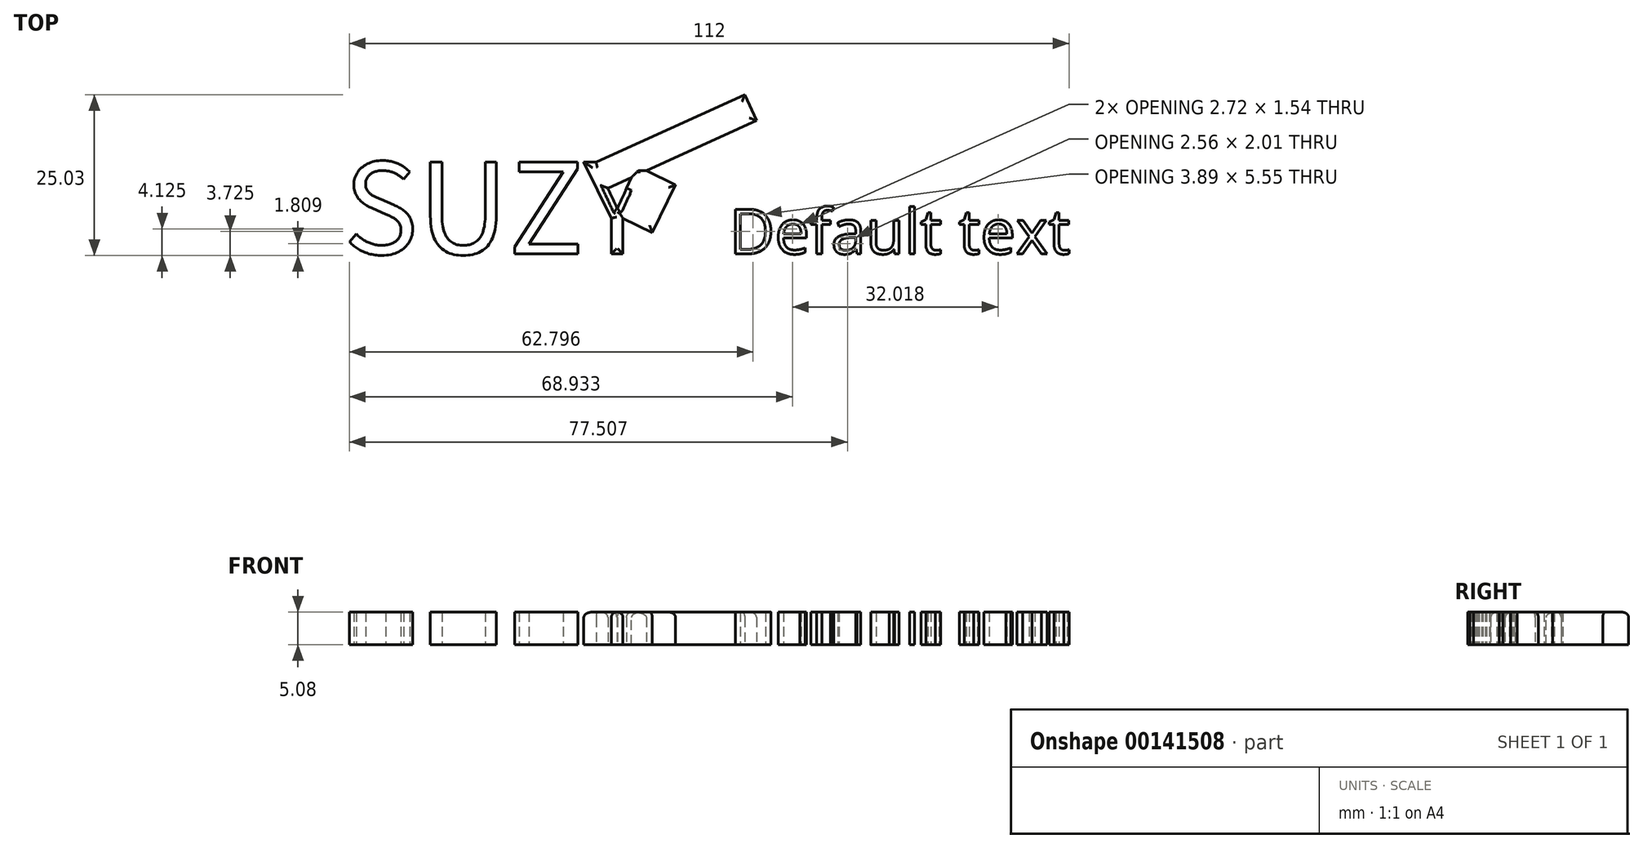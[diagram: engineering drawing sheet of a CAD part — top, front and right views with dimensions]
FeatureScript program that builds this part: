
annotation { "Feature Type Name" : "Feature", "Feature Type Description" : "" }
export const myFeature = defineFeature(function(context is Context, id is Id, definition is map)
    precondition{}
    {
        {
            var Q0;
            Q0=qCreatedBy(makeId("Top.planeOp"),FACE);
            var sketch = newSketch(context, id + "F0", { "sketchPlane" : qUnion([Q0])});
            skText(sketch, "E0", { "text": "SUZY", "fontName": "NotoSansCJKjp-Regular.otf"});
            skText(sketch, "E1", { "text": "Default text", "fontName": "OpenSans-Regular.ttf"});
            skPoint(sketch, "E1.secondSnap0", {"position": v(19.76, 18.92) * mm});
            const initialGuessF0  = {"E0": [-0.0291, 0.01191, 1, 0, 0.01402], "E1": [0.03091, 0.01191, 1, 0, 0.00701]};
            skSetInitialGuess(sketch, initialGuessF0);
            skSolve(sketch);
        }
        {
            var Q0;
            Q0 = qSketchRegion(id + "F0", true);
            extrude(context, id + "F1", {"entities" : qUnion([Q0]), "depth" : 5.08 * mm});
        }
        {
            var Q0;
            Q0=makeQuery(id+"F1.opExtrude","SWEPT_FACE",FACE,{"disambiguationData":[OSD([sQuery(id+"F0.wireOp",EDGE,"E0.sketch_text.stroke-44")])]});
            extrude(context, id + "F2", {"entities" : qUnion([Q0]), "operationType" : NewBodyOperationType.ADD, "depth" : 25.4 * mm});
        }
        {
            var Q0;
            Q0=makeQuery(id+"F1.opExtrude","SWEPT_FACE",FACE,{"disambiguationData":[OSD([sQuery(id+"F0.wireOp",EDGE,"E0.sketch_text.stroke-38")])]});
            extrude(context, id + "F3", {"entities" : qUnion([Q0]), "operationType" : NewBodyOperationType.ADD, "depth" : 5.08 * mm});
        }
        {
            var Q0;
            {var subQ0=sQuery(id+"F0.wireOp",EDGE,"E0.sketch_text.stroke-38");var subQ1=sQuery(id+"F0.wireOp",EDGE,"E0.sketch_text.stroke-44");Q0=makeQuery(id+"F3.boolean.opBoolean","MERGE",FACE,{"derivedFrom":[makeQuery(id+"F2.boolean.opBoolean","MERGE",FACE,{"derivedFrom":[makeQuery(id+"F1.opExtrude","CAP_FACE",FACE,{"disambiguationData":[OSD([sQuery(id+"F0.wireOp",EDGE,"E0.sketch_text.stroke-36"),sQuery(id+"F0.wireOp",EDGE,"E0.sketch_text.stroke-37"),subQ0,sQuery(id+"F0.wireOp",EDGE,"E0.sketch_text.stroke-39"),sQuery(id+"F0.wireOp",EDGE,"E0.sketch_text.stroke-40"),sQuery(id+"F0.wireOp",EDGE,"E0.sketch_text.stroke-41"),sQuery(id+"F0.wireOp",EDGE,"E0.sketch_text.stroke-42"),sQuery(id+"F0.wireOp",EDGE,"E0.sketch_text.stroke-43"),subQ1,sQuery(id+"F0.wireOp",EDGE,"E0.sketch_text.stroke-45"),sQuery(id+"F0.wireOp",EDGE,"E0.sketch_text.stroke-46"),sQuery(id+"F0.wireOp",EDGE,"E0.sketch_text.stroke-47")])],"isStart":false}),makeQuery(id+"F2.opExtrude","SWEPT_FACE",FACE,{"disambiguationData":[OSD([subQ1]),TDD([makeQuery(id+"F1.opExtrude","CAP_EDGE",EDGE,{"disambiguationData":[OSD([subQ1])],"isStart":false})])]})]}),makeQuery(id+"F3.opExtrude","SWEPT_FACE",FACE,{"disambiguationData":[OSD([subQ0]),TDD([makeQuery(id+"F1.opExtrude","CAP_EDGE",EDGE,{"disambiguationData":[OSD([subQ0])],"isStart":false})])]})]});}
            var Q1;
            {var subQ0=sQuery(id+"F0.wireOp",EDGE,"E0.sketch_text.stroke-44");var subQ1=sQuery(id+"F0.wireOp",EDGE,"E0.sketch_text.stroke-43");var subQ2=sQuery(id+"F0.wireOp",EDGE,"E0.sketch_text.stroke-38");Q1=makeQuery(id+"F2.boolean.opBoolean","SPLIT",EDGE,{"disambiguationData":[TD([makeQuery(id+"F1.opExtrude","SWEPT_FACE",FACE,{"disambiguationData":[OSD([subQ2])]})])],"derivedFrom":makeQuery(id+"F2.opExtrude","SWEPT_EDGE",EDGE,{"disambiguationData":[OSD([subQ1,subQ0]),TDD([makeQuery(id+"F1.opExtrude","CAP_VERTEX",VERTEX,{"disambiguationData":[OSD([subQ1,subQ0])],"isStart":false})])]})});}
            fillet(context, id + "F4", {"entities" : qUnion([Q0, Q1]), "radius" : 0.85 * mm, "tangentPropagation" : true, "allowEdgeOverflow" : false});
        }
    });
